# Revit family: РИДАН_Кран шаровой BVS-R из нержавеющей стали
name_source: partatom
category: Арматура трубопроводов
units: mm (PartAtom-declared; Revit-internal decimal feet)

## family parameters
Всегда вертикально = Да
На основе рабочей плоскости = Нет
Общий = Нет
При загрузке вырезать с полостями = Нет
Размер круглого соединителя = Использовать диаметр
Тип детали = Вставляется

## types (8) — shared parameters
ADSK_Версия Revit = 2019
ADSK_Версия семейства = 1.0
ADSK_Единица измерения = шт.
ADSK_Завод-изготовитель = ООО «Ридан-Трейд»
ADSK_Количество = 1
ADSK_Потеря давления жидкости = 0.0 Па
ADSK_Расход жидкости = 0.000 м³/ч
LT = BVS-R
URL = https://ridan.ru
Изготовитель = ООО «Ридан-Трейд»

## per-type parameters (varying)
| type | ADSK_Диаметр условный | ADSK_Код изделия | ADSK_Марка | ADSK_Масса | ADSK_Наименование | ADSK_Пропускная способность | a | b | c | d | e | f | g | h |
| DN 8 | 8 мм | 082X4600R | BVS-R DN8 | 0.06 | Кран шаровой BVS-R из нержавеющей стали PN63, Tmax=180C, ВР, DN8 | 4.700 м³/ч | 6 мм | 14 мм | 61 мм | 11 мм | 8 мм | 11 мм | 17 мм | 15 мм |
| DN 10 | 10 мм | 082X4601R | BVS-R DN10 | 0.09 | Кран шаровой BVS-R из нержавеющей стали PN63, Tmax=180C, ВР, DN10 | 8.500 м³/ч | 8 мм | 15 мм | 60 мм | 14 мм | 10 мм | 13 мм | 21 мм | 17 мм |
| DN 15 | 15 мм | 082X4602R | BVS-R DN15 | 0.15 | Кран шаровой BVS-R из нержавеющей стали PN63, Tmax=180C, ВР, DN15 | 13.200 м³/ч | 9 мм | 19 мм | 61 мм | 16 мм | 12 мм | 13 мм | 25 мм | 21 мм |
| DN 20 | 20 мм | 082X4603R | BVS-R DN20 | 0.22 | Кран шаровой BVS-R из нержавеющей стали PN63, Tmax=180C, ВР, DN20 | 17.000 м³/ч | 11 мм | 19 мм | 61 мм | 19 мм | 15 мм | 16 мм | 32 мм | 26 мм |
| DN 25 | 25 мм | 082X4604R | BVS-R DN25 | 0.36 | Кран шаровой BVS-R из нержавеющей стали PN63, Tmax=180C, ВР, DN25 | 30.200 м³/ч | 12 мм | 24 мм | 61 мм | 23 мм | 18 мм | 16 мм | 38 мм | 34 мм |
| DN 32 | 32 мм | 082X4605R | BVS-R DN32 | 0.55 | Кран шаровой BVS-R из нержавеющей стали PN63, Tmax=180C, ВР, DN32 | 45.200 м³/ч | 13 мм | 25 мм | 60 мм | 28 мм | 23 мм | 18 мм | 47 мм | 42 мм |
| DN 40 | 40 мм | 082X4606R | BVS-R DN40 | 0.86 | Кран шаровой BVS-R из нержавеющей стали PN63, Tmax=180C, ВР, DN40 | 69.700 м³/ч | 16 мм | 26 мм | 61 мм | 32 мм | 26 мм | 20 мм | 53 мм | 48 мм |
| DN 50 | 50 мм | 082X4607R | BVS-R DN50 | 1.29 | Кран шаровой BVS-R из нержавеющей стали PN63, Tmax=180C, ВР, DN50 | 128.200 м³/ч | 21 мм | 28 мм | 61 мм | 37 мм | 32 мм | 21 мм | 65 мм | 60 мм |
